# Revit family: Kabelrinne BKRS 1010 90L FS
name_source: partatom
category: Generic Models
revit_build: Autodesk Revit 2017 (Build: 20190508_0315(x64)
units: mm (PartAtom-declared; Revit-internal decimal feet)

## family parameters
Always vertical = Yes
Can host rebar = No
Cut with Voids When Loaded = No
Part Type = Normal
Room Calculation Point = No
Round Connector Dimension = Use Diameter
Shared = No
Work Plane-Based = No

## types (1)
- BKRS 1010 90L FS
    Article Type = BKRS 1010 90L FS
    Cut's number = 2
    Cut's number 2 = 3
    Cut's number 3 = 19
    GTIN = 4012196710225
    Manufacturer = OBO BETTERMANN
    Manufacturer Art.No. = 6061918
    Material = Strip galvanised
    URL = http://www.obo-bettermann.com
    Width = 100 mm  [stored 0.328084 ft]

note: [stored X ft] marks values corroborated as IEEE doubles in the binary element streams (Revit-internal decimal feet)

## geometry (parser evidence)
native form markers: Sweep x2
no freeform markers — native parametric forms only
